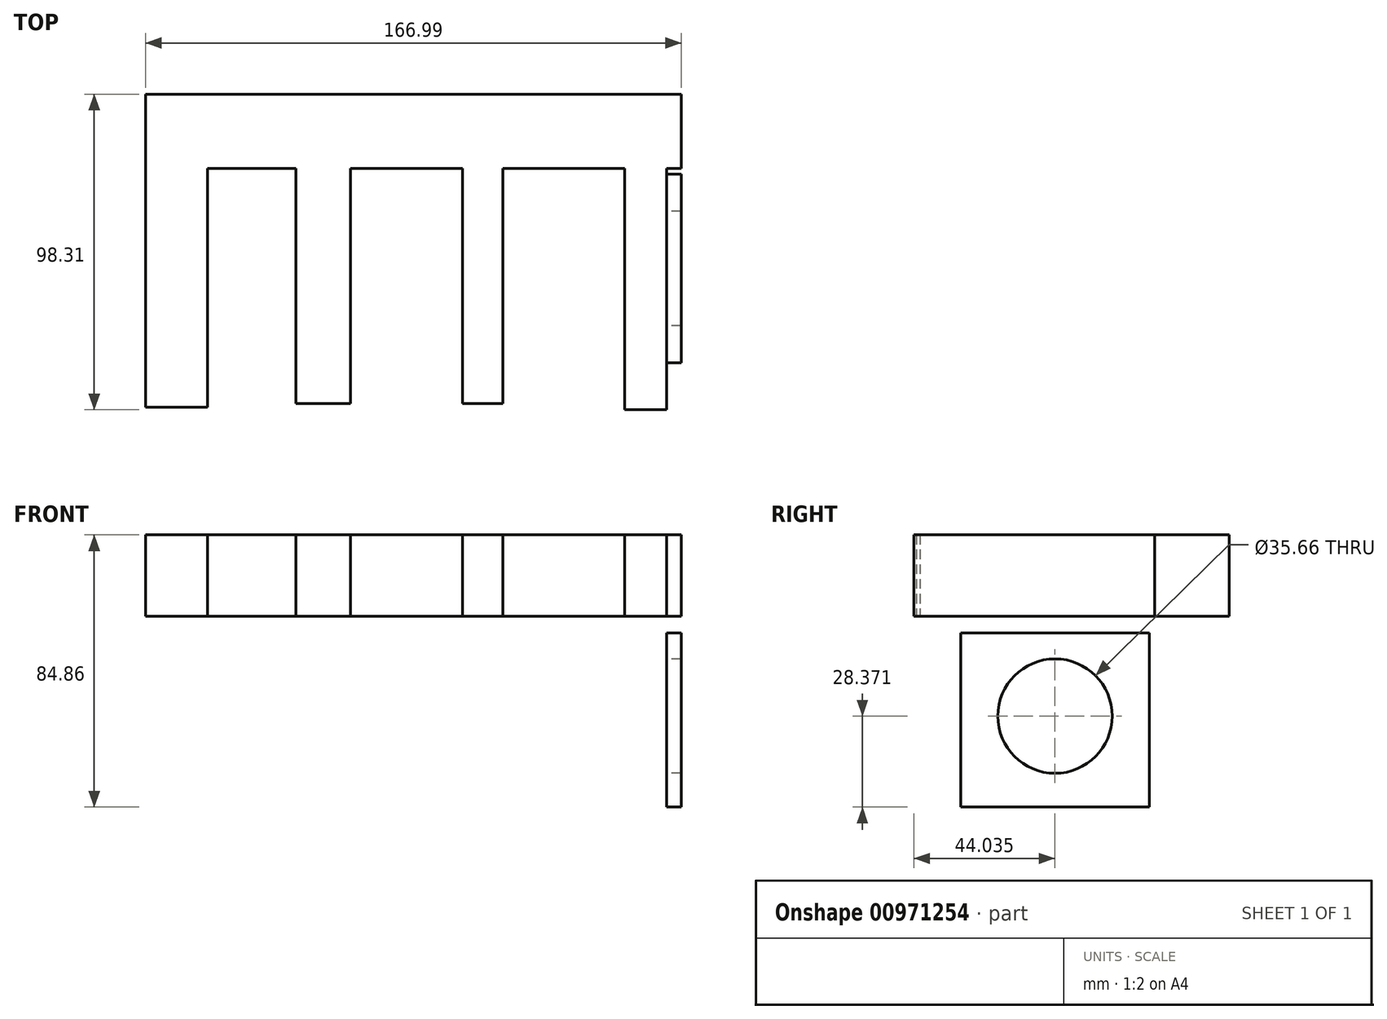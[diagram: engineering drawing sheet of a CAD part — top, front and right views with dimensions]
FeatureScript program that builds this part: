
annotation { "Feature Type Name" : "Feature", "Feature Type Description" : "" }
export const myFeature = defineFeature(function(context is Context, id is Id, definition is map)
    precondition{}
    {
        {
            var Q0;
            Q0=qCreatedBy(makeId("Top.planeOp"),FACE);
            var sketch = newSketch(context, id + "F0", { "sketchPlane" : qUnion([Q0])});
            skLineSegment(sketch, "E0.bottom", {"start": v(-86.49, 44.86) * mm, "end": v(80.5, 44.86) * mm});
            skLineSegment(sketch, "E0.top", {"start": v(-86.49, 21.7) * mm, "end": v(80.5, 21.7) * mm});
            skLineSegment(sketch, "E0.left", {"start": v(-86.49, 44.86) * mm, "end": v(-86.49, 21.7) * mm});
            skLineSegment(sketch, "E0.right", {"start": v(80.5, 44.86) * mm, "end": v(80.5, 21.7) * mm});
            skLineSegment(sketch, "E1.bottom", {"start": v(-86.49, 21.7) * mm, "end": v(-67.21, 21.7) * mm});
            skLineSegment(sketch, "E1.top", {"start": v(-86.49, -52.64) * mm, "end": v(-67.21, -52.64) * mm});
            skLineSegment(sketch, "E1.left", {"start": v(-86.49, 21.7) * mm, "end": v(-86.49, -52.64) * mm});
            skLineSegment(sketch, "E1.right", {"start": v(-67.21, 21.7) * mm, "end": v(-67.21, -52.64) * mm});
            skLineSegment(sketch, "E2.bottom", {"start": v(-39.68, 21.7) * mm, "end": v(-22.67, 21.7) * mm});
            skLineSegment(sketch, "E2.top", {"start": v(-39.68, -51.5) * mm, "end": v(-22.67, -51.5) * mm});
            skLineSegment(sketch, "E2.left", {"start": v(-39.68, 21.7) * mm, "end": v(-39.68, -51.5) * mm});
            skLineSegment(sketch, "E2.right", {"start": v(-22.67, 21.7) * mm, "end": v(-22.67, -51.5) * mm});
            skLineSegment(sketch, "E3.bottom", {"start": v(12.3, 21.7) * mm, "end": v(24.94, 21.7) * mm});
            skLineSegment(sketch, "E3.top", {"start": v(12.3, -51.5) * mm, "end": v(24.94, -51.5) * mm});
            skLineSegment(sketch, "E3.left", {"start": v(12.3, 21.7) * mm, "end": v(12.3, -51.5) * mm});
            skLineSegment(sketch, "E3.right", {"start": v(24.94, 21.7) * mm, "end": v(24.94, -51.5) * mm});
            skLineSegment(sketch, "E4.bottom", {"start": v(62.84, 21.7) * mm, "end": v(75.96, 21.7) * mm});
            skLineSegment(sketch, "E4.top", {"start": v(62.84, -53.45) * mm, "end": v(75.96, -53.45) * mm});
            skLineSegment(sketch, "E4.left", {"start": v(62.84, 21.7) * mm, "end": v(62.84, -53.45) * mm});
            skLineSegment(sketch, "E4.right", {"start": v(75.96, 21.7) * mm, "end": v(75.96, -53.45) * mm});
            skSolve(sketch);
        }
        {
            var Q0;
            Q0=qCreatedBy(makeId("Right.planeOp"),FACE);
            var sketch = newSketch(context, id + "F1", { "sketchPlane" : qUnion([Q0])});
            skLineSegment(sketch, "E5.bottom", {"start": v(-38.82, -17.87) * mm, "end": v(19.99, -17.87) * mm});
            skLineSegment(sketch, "E5.top", {"start": v(-38.82, -72.16) * mm, "end": v(19.99, -72.16) * mm});
            skLineSegment(sketch, "E5.left", {"start": v(-38.82, -17.87) * mm, "end": v(-38.82, -72.16) * mm});
            skLineSegment(sketch, "E5.right", {"start": v(19.99, -17.87) * mm, "end": v(19.99, -72.16) * mm});
            skCircle(sketch, "E6", {"center": v(-9.42, -43.79) * mm, "radius": 17.83 * mm});
            skPoint(sketch, "E6.centerSnap0", {"position": v(-9.42, -72.16) * mm});
            skSolve(sketch);
        }
        {
            var Q0;
            Q0=qSketchRegion(id+"F0",true);
            extrude(context, id + "F2", {"entities" : qUnion([Q0]), "depth" : 25.4 * mm, "symmetric" : true});
        }
        {
            var Q0;
            Q0=makeQuery(id+"F1.imprint","IMPRINT",FACE,{"disambiguationData":[TD([[makeQuery(id+"F1.imprint","IMPRINT",EDGE,{"derivedFrom":sQuery(id+"F1.wireOp",EDGE,"E5.bottom")}),-1.0]])]});
            var Q1;
            Q1=makeQuery(id+"F2.opExtrude","SWEPT_FACE",FACE,{"disambiguationData":[OSD([sQuery(id+"F0.wireOp",EDGE,"E0.right")])]});
            var Q2;
            Q2=makeQuery(id+"F2.opExtrude","CAP_VERTEX",VERTEX,{"disambiguationData":[OSD([sQuery(id+"F0.wireOp",EDGE,"E0.top"),sQuery(id+"F0.wireOp",EDGE,"E0.right")])],"isStart":true});
            var Q3;
            Q3=makeQuery(id+"F2.opExtrude","SWEPT_FACE",FACE,{"disambiguationData":[OSD([sQuery(id+"F0.wireOp",EDGE,"E4.right")])]});
            var Q4;
            Q4=makeQuery(id+"F2.opExtrude","CAP_VERTEX",VERTEX,{"disambiguationData":[OSD([sQuery(id+"F0.wireOp",EDGE,"E0.top"),sQuery(id+"F0.wireOp",EDGE,"E4.bottom"),sQuery(id+"F0.wireOp",EDGE,"E4.right")])],"isStart":true});
            extrude(context, id + "F3", {"entities" : qUnion([Q0]), "endBound" : BoundingType.UP_TO_VERTEX, "endBoundEntityFace" : qUnion([Q1]), "endBoundEntityVertex" : qUnion([Q2]), "depth" : 80.62 * mm, "hasSecondDirection" : true, "secondDirectionBound" : BoundingType.UP_TO_VERTEX, "secondDirectionOppositeDirection" : false, "secondDirectionBoundEntityFace" : qUnion([Q3]), "secondDirectionBoundEntityVertex" : qUnion([Q4]), "secondDirectionDepth" : 75.95 * mm});
        }
        {
            var Q0;
            {var subQ0=sQuery(id+"F0.wireOp",EDGE,"E0.top");Q0=makeQuery(id+"F2.opExtrude","SWEPT_FACE",FACE,{"disambiguationData":[OSD([subQ0]),TDD([makeQuery(id+"F0.imprint","IMPRINT",EDGE,{"disambiguationData":[TD([[makeQuery(id+"F0.imprint","INTERSECT",VERTEX,{"derivedFrom":[subQ0,sQuery(id+"F0.wireOp",EDGE,"E3.bottom"),sQuery(id+"F0.wireOp",EDGE,"E3.right")]}),-1.0]])],"derivedFrom":subQ0})])]});}
            cPlane(context, id + "F4", {"entities" : qUnion([Q0]), "cplaneType" : CPlaneType.OFFSET, "offset" : 38.6 * mm, "width" : 152.4 * mm, "height" : 152.4 * mm});
        }
    });
